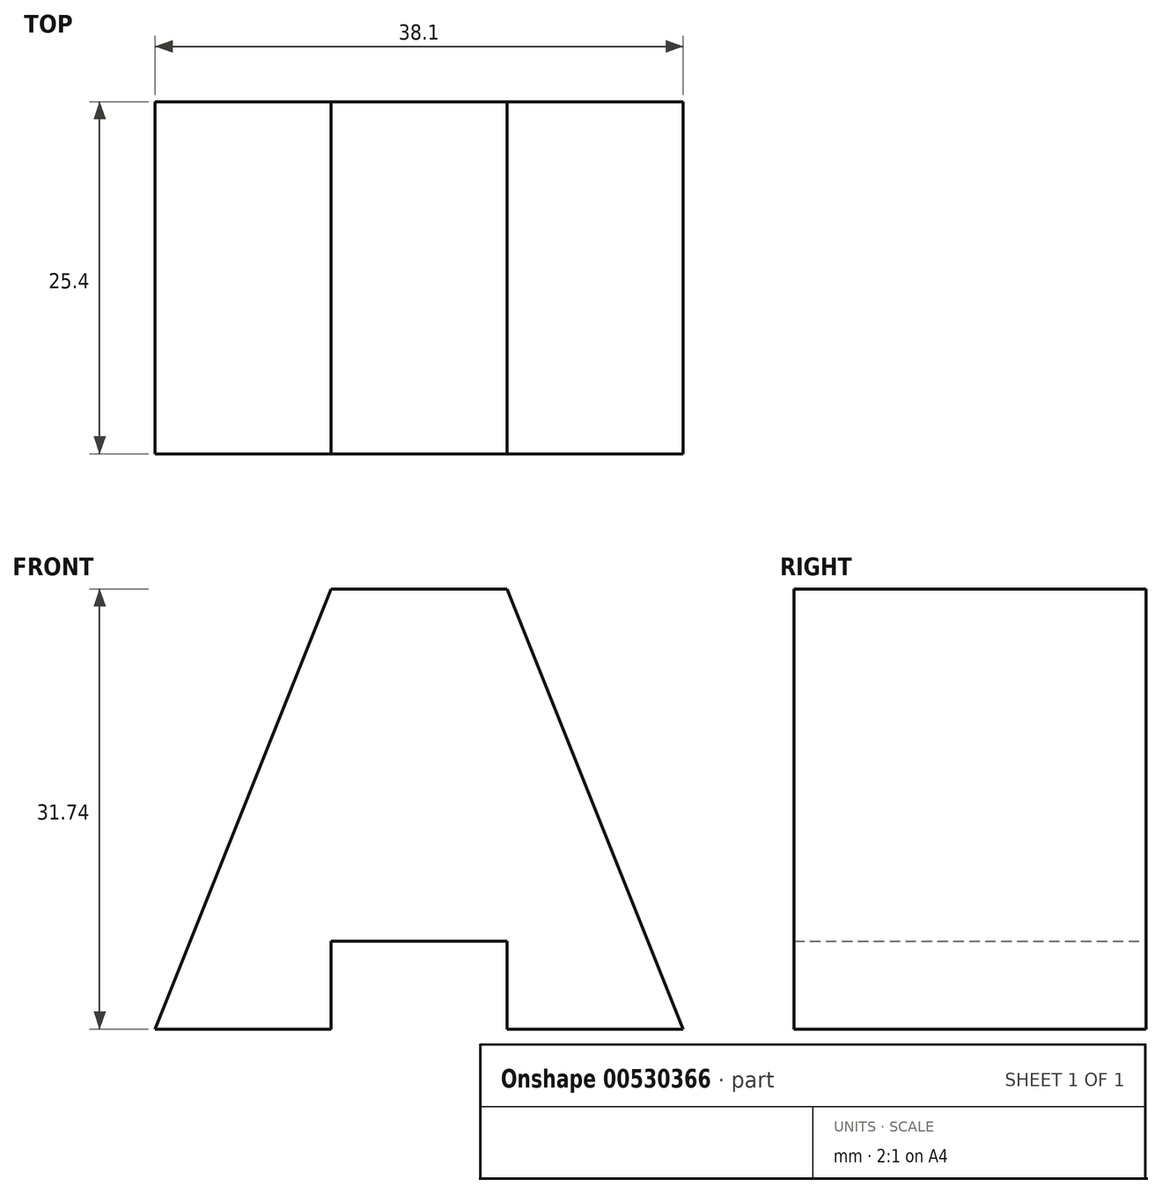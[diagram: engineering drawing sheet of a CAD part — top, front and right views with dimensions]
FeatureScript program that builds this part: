
annotation { "Feature Type Name" : "Feature", "Feature Type Description" : "" }
export const myFeature = defineFeature(function(context is Context, id is Id, definition is map)
    precondition{}
    {
        {
            var Q0;
            Q0=qCreatedBy(makeId("Front.planeOp"),FACE);
            var sketch = newSketch(context, id + "F0", { "sketchPlane" : qUnion([Q0])});
            skLineSegment(sketch, "E0", {"start": v(0, 0) * mm, "end": v(-12.7, 31.74) * mm});
            skLineSegment(sketch, "E1", {"start": v(-12.7, 31.74) * mm, "end": v(-25.4, 31.74) * mm});
            skLineSegment(sketch, "E2", {"start": v(-25.4, 31.74) * mm, "end": v(-38.1, 0) * mm});
            skLineSegment(sketch, "E3", {"start": v(-38.1, 0) * mm, "end": v(-25.4, 0) * mm});
            skLineSegment(sketch, "E4", {"start": v(-25.4, 0) * mm, "end": v(-25.4, 6.35) * mm});
            skLineSegment(sketch, "E5", {"start": v(-25.4, 6.35) * mm, "end": v(-12.7, 6.35) * mm});
            skLineSegment(sketch, "E6", {"start": v(-12.7, 6.35) * mm, "end": v(-12.7, 0) * mm});
            skLineSegment(sketch, "E7", {"start": v(-12.7, 0) * mm, "end": v(0, 0) * mm});
            skSolve(sketch);
        }
        {
            var Q0;
            Q0 = qSketchRegion(id + "F0", true);
            extrude(context, id + "F1", {"entities" : qUnion([Q0]), "depth" : 25.4 * mm, "offsetDistance" : 25.4 * mm});
        }
    });
